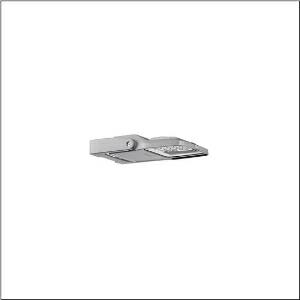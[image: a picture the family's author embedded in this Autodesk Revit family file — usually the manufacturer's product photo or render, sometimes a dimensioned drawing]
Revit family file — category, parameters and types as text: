
# Revit family: floodlight_fl_21_iq_micro___pl64_5xa7762a4e2a_da81
name_source: partatom
category: Lighting Fixtures
units: mm (PartAtom-declared; Revit-internal decimal feet)

## family parameters
Cut with Voids When Loaded = No
Host = Face
Light Source = No
Part Type = Normal
Room Calculation Point = No
Round Connector Dimension = Use Diameter
Shared = No

## types (1)
- --- (1 x LED, 2980 lm, 23.1 W, 4000K)
    Apparent Load = 23 VA
    CIE Flux Codes = 28 80 98 100 100
    Color Rendering = 70
    Color Temperature = 4000K
    Default Elevation = 1800 mm
    Description = Floodlight FL 21 iQ micro, floodlight, primary light control with lens, of PMMA, primary optical cover: protective disc, of toughened safety glass, transparent, light distribution: PL64, light emission: direct distribution, installation type: surface-mounted, LED, High Power LED, rated luminous flux: 2.980lm, luminous efficacy: 129lm/W, light colour: 740, colour temperature: 4000K, control gear: iQ Street-Remote/DALI, control: Auto-Match, Temp-Guard, Night-Set, Smart-Wire, Desk-Remote (wireless, voltage-free reading and setting of iQ features in the workshop via application-optimized NFC function/RFID function), optimised constant luminous flux control (CLO 2.0), Street-Remote, with terminal, 6-pole, mains connection: 220..240V, AC, 50/60Hz, start of lifetime: 23W, end of service life: 24W, reduction: 11W, luminaire housing, of diecast aluminium, powder-coated, Siteco® metallic grey (DB 702S), corrosivity category C5 mid according to DIN EN ISO 12944, suitable for swimming pools, chlorine-resistant, sealing non-destructively replaceable, design bracket, of diecast aluminium, powder-coated, Siteco® metallic grey (DB 702S), protection rating (complete): IP66, insulation class (complete): insulation class II (safety insulation), certification: CE, ENEC, VDE, protection symbol: D, impact resistance: IK07, permissible operating ambient temperature: -40..+40°C, permissible operating ambient temperature for outdoor applications: -40..+50°C, standard: DIN EN 12944, LABS conformity tested according to VDMA 24364:2018-05, packaging unit: 1 piece

Light Distribution: PL64
    Height = 65 mm
    Lamp = 1 x LED
    Lamp Light Flux = 2980 lm
    Lamp Power = 23.1 W
    Lamp count = 1
    Length = 312 mm
    Luminous efficacy = 129 lm/W
    Manufacturer = Siteco
    ModVariant = No
    Model = 5XA7762A4E2A
    Mounting Place = Wall
    Mounting Type = Surface mounted
    Number of Poles = 1
    OnlyDefault = Yes
    Power Factor = 1
    Product Name = Floodlight FL 21 iQ micro | PL64
    Product group = floodlight | wall mounted
    ProductGroupID = 2001
    Protection Class = Protection class II
    Protection Degree = IP 66
    RLX_Detail_Level = 1
    RLX_Emergency_Light_Flux = 0 lm
    RLX_Emergency_Type = 0
    RLX_Emergency_Type_DB = No
    RlxData = <blob elided: 97417 chars, md5=022f695f>
    Socket = socket
    Standby Power = 0 W
    System Light Flux = 2980 lm
    System Power = 23 W
    Type Comments = factory setting: luminous flux: 100 % | dim-lin: 254 | 455 mA
    Type Image = l_1006878.jpg
    URL = http://relux.com
    VarID = @adj_201933
    Voltage = 0 V
    Weight = 0.00 kg
    Width = 230 mm

## geometry (parser evidence)
native form markers: Blend x4, Sweep x13
no freeform markers — native parametric forms only
